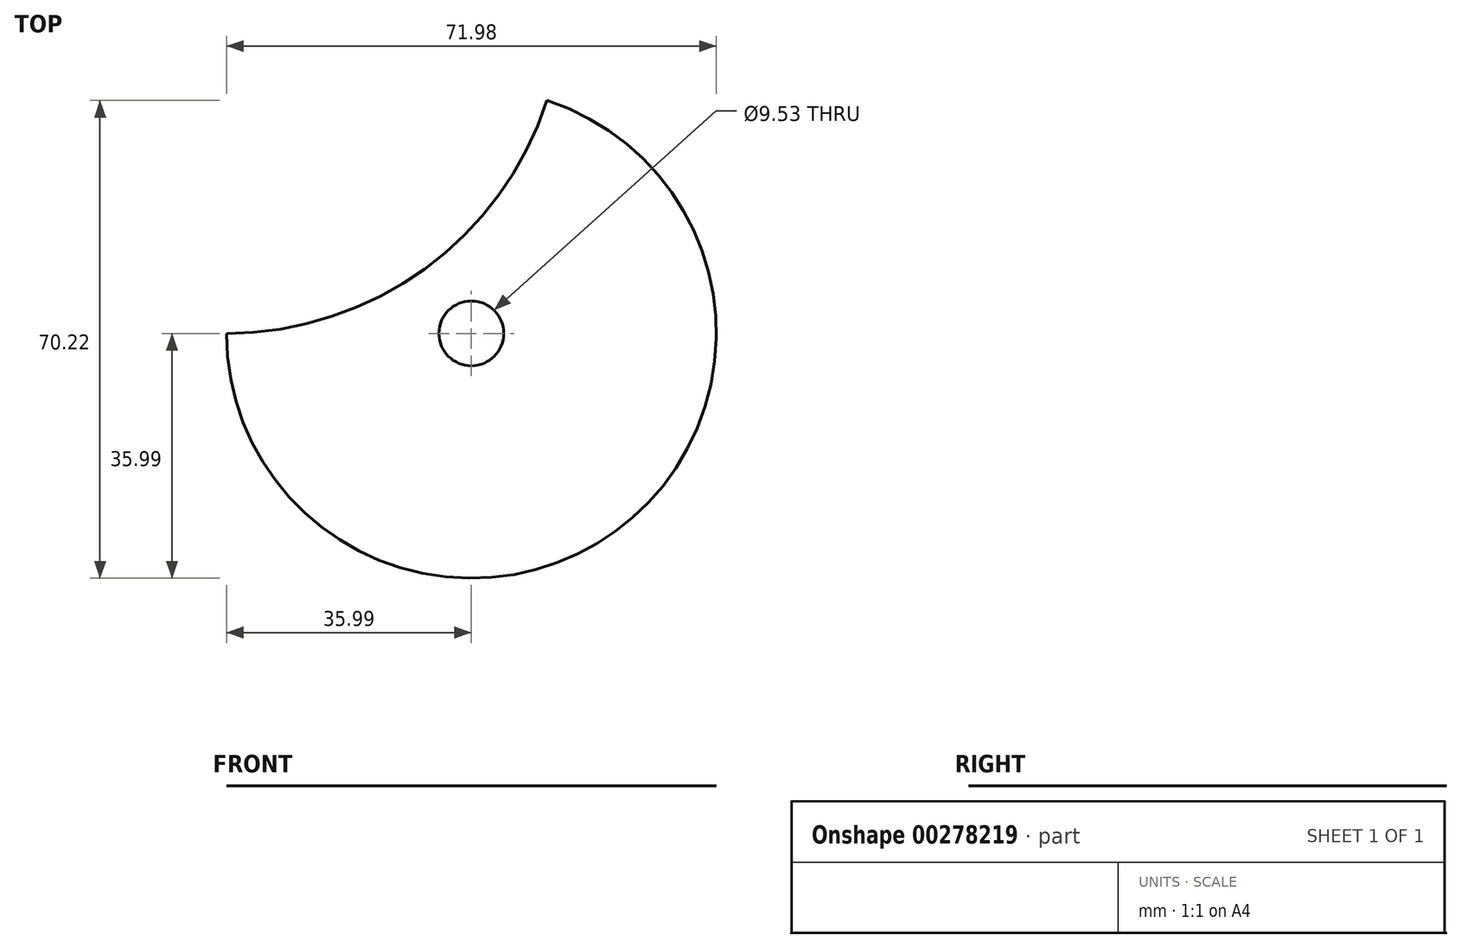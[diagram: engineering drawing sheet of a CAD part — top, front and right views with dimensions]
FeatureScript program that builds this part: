
annotation { "Feature Type Name" : "Feature", "Feature Type Description" : "" }
export const myFeature = defineFeature(function(context is Context, id is Id, definition is map)
    precondition{}
    {
        {
            var Q0;
            Q0=qCreatedBy(makeId("Top.planeOp"),FACE);
            var sketch = newSketch(context, id + "F0", { "sketchPlane" : qUnion([Q0])});
            skLineSegment(sketch, "E0", {"start": v(0, 0) * mm, "end": v(-86.44, 0) * mm});
            skLineSegment(sketch, "E1", {"start": v(-86.44, 0) * mm, "end": v(-29.88, 41.08) * mm});
            skLineSegment(sketch, "E2", {"start": v(-29.88, 41.08) * mm, "end": v(-6.88, 9.46) * mm});
            skCircle(sketch, "E3", {"center": v(0, 0) * mm, "radius": 58.9 * mm});
            skArc(sketch, "E4", {"start": v(-21.15, 29.12) * mm, "mid": v(-21.16, 29.11) * mm, "end": v(-21.17, 29.1) * mm});
            skLineSegment(sketch, "E5", {"start": v(0, 0) * mm, "end": v(-36, 0) * mm});
            skLineSegment(sketch, "E6", {"start": v(-36, 0) * mm, "end": v(-36, 49.54) * mm});
            skLineSegment(sketch, "E7", {"start": v(-36, 49.54) * mm, "end": v(-21.15, 29.12) * mm});
            skCircle(sketch, "E8", {"center": v(-36, 49.54) * mm, "radius": 49.54 * mm});
            skArc(sketch, "E9.trimOffspring", {"start": v(-36, 0) * mm, "mid": v(21.15, -29.12) * mm, "end": v(11.12, 34.23) * mm});
            skCircle(sketch, "E10", {"center": v(0, 0) * mm, "radius": 4.76 * mm});
            skCircle(sketch, "E11", {"center": v(-29.88, 41.08) * mm, "radius": 4.76 * mm});
            skSolve(sketch);
        }
        {
            var Q0;
            {var subQ0=sQuery(id+"F0.wireOp",EDGE,"E9.trimOffspring");Q0=makeQuery(id+"F0.imprint","IMPRINT",FACE,{"disambiguationData":[TD([[makeQuery(id+"F0.imprint","IMPRINT",EDGE,{"derivedFrom":subQ0}),1.0]])]});}
            var Q1;
            {var subQ0=sQuery(id+"F0.wireOp",EDGE,"E8");var subQ1=sQuery(id+"F0.wireOp",EDGE,"E2");var subQ2=makeQuery(id+"F0.imprint","INTERSECT",VERTEX,{"derivedFrom":[subQ1,subQ0]});Q1=makeQuery(id+"F0.imprint","IMPRINT",FACE,{"disambiguationData":[TD([[makeQuery(id+"F0.imprint","IMPRINT",EDGE,{"disambiguationData":[TD([[subQ2,-1.0]])],"derivedFrom":subQ1}),-1.0]])]});}
            extrude(context, id + "F1", {"entities" : qUnion([Q0, Q1]), "depth" : 1 / 203.2 * mm});
        }
    });
